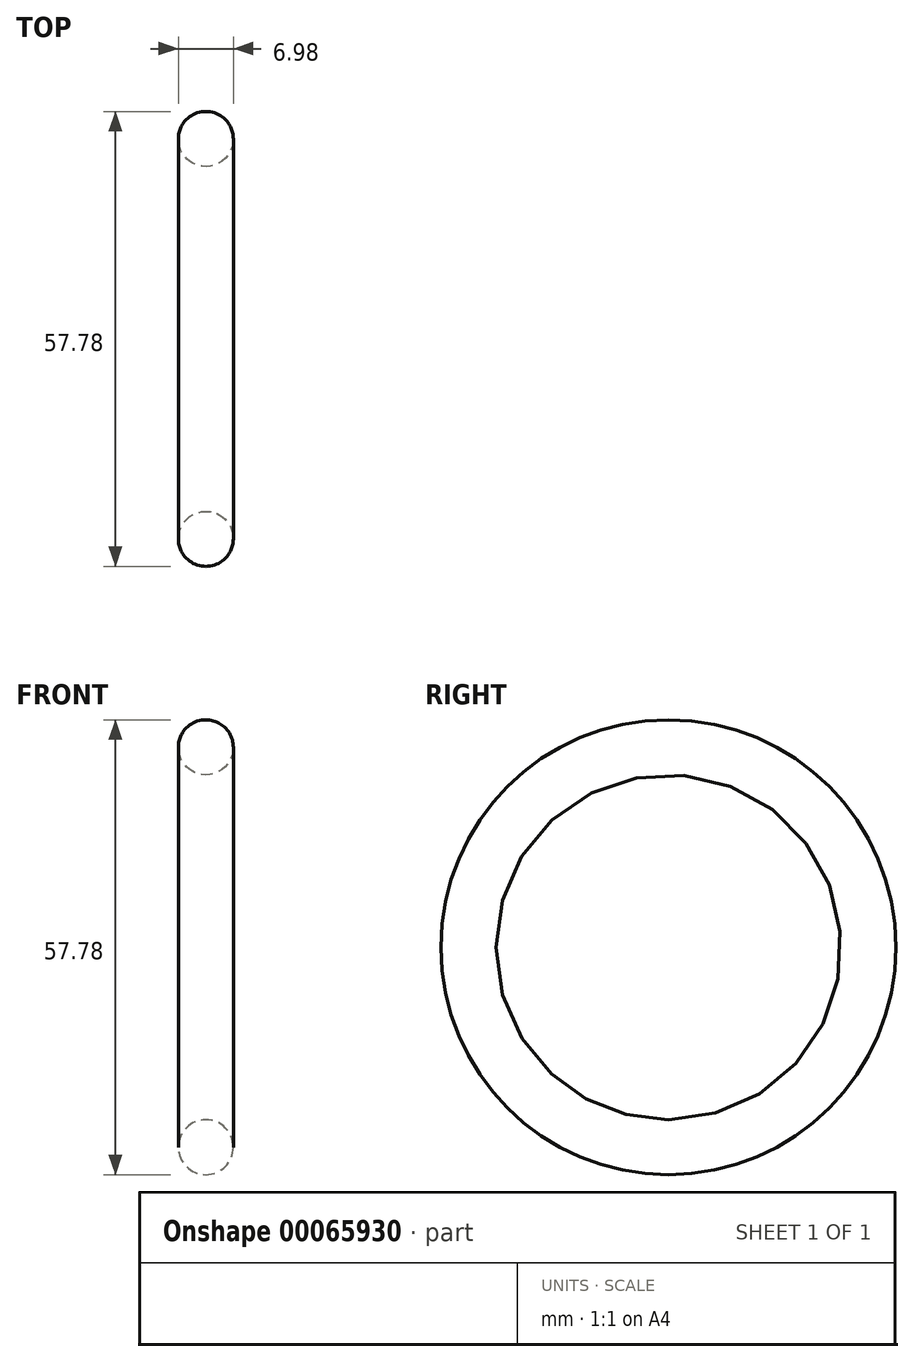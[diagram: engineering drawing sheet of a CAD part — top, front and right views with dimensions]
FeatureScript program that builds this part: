
annotation { "Feature Type Name" : "Feature", "Feature Type Description" : "" }
export const myFeature = defineFeature(function(context is Context, id is Id, definition is map)
    precondition{}
    {
        {
            var Q0;
            Q0=qCreatedBy(makeId("Front.planeOp"),FACE);
            var sketch = newSketch(context, id + "F0", { "sketchPlane" : qUnion([Q0])});
            skLineSegment(sketch, "E0", {"start": v(0, 0) * mm, "end": v(-6.06, 0) * mm, "construction": true});
            skCircle(sketch, "E1", {"center": v(0, 25.4) * mm, "radius": 3.5 * mm});
            skSolve(sketch);
        }
        {
            var Q0;
            Q0=makeQuery(id+"F0.imprint","IMPRINT",FACE,{"disambiguationData":[TD([[makeQuery(id+"F0.imprint","IMPRINT",EDGE,{"derivedFrom":sQuery(id+"F0.wireOp",EDGE,"E1")}),1.0]])]});
            var Q1;
            Q1=sQuery(id+"F0.wireOp",EDGE,"E0");
            revolve(context, id + "F1", {"entities" : qUnion([Q0]), "axis" : qUnion([Q1]), "revolveType" : RevolveType.FULL});
        }
    });
